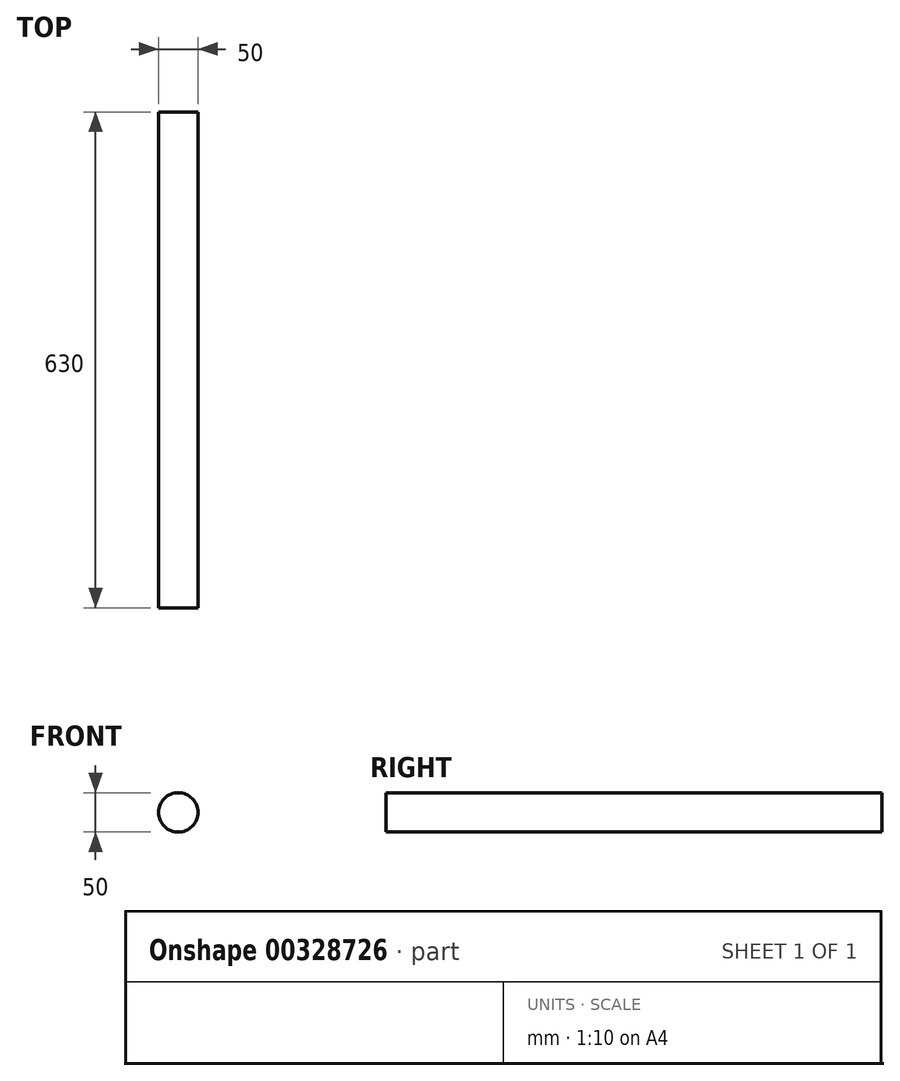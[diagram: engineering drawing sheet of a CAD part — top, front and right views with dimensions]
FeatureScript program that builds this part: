
annotation { "Feature Type Name" : "Feature", "Feature Type Description" : "" }
export const myFeature = defineFeature(function(context is Context, id is Id, definition is map)
    precondition{}
    {
        {
            var Q0;
            Q0=qCreatedBy(makeId("Front.planeOp"),FACE);
            var sketch = newSketch(context, id + "F0", { "sketchPlane" : qUnion([Q0])});
            skCircle(sketch, "E0", {"center": v(0, 0) * mm, "radius": 25 * mm});
            skSolve(sketch);
        }
        {
            var Q0;
            Q0 = qSketchRegion(id + "F0", true);
            extrude(context, id + "F1", {"entities" : qUnion([Q0]), "depth" : 630 * mm});
        }
    });
